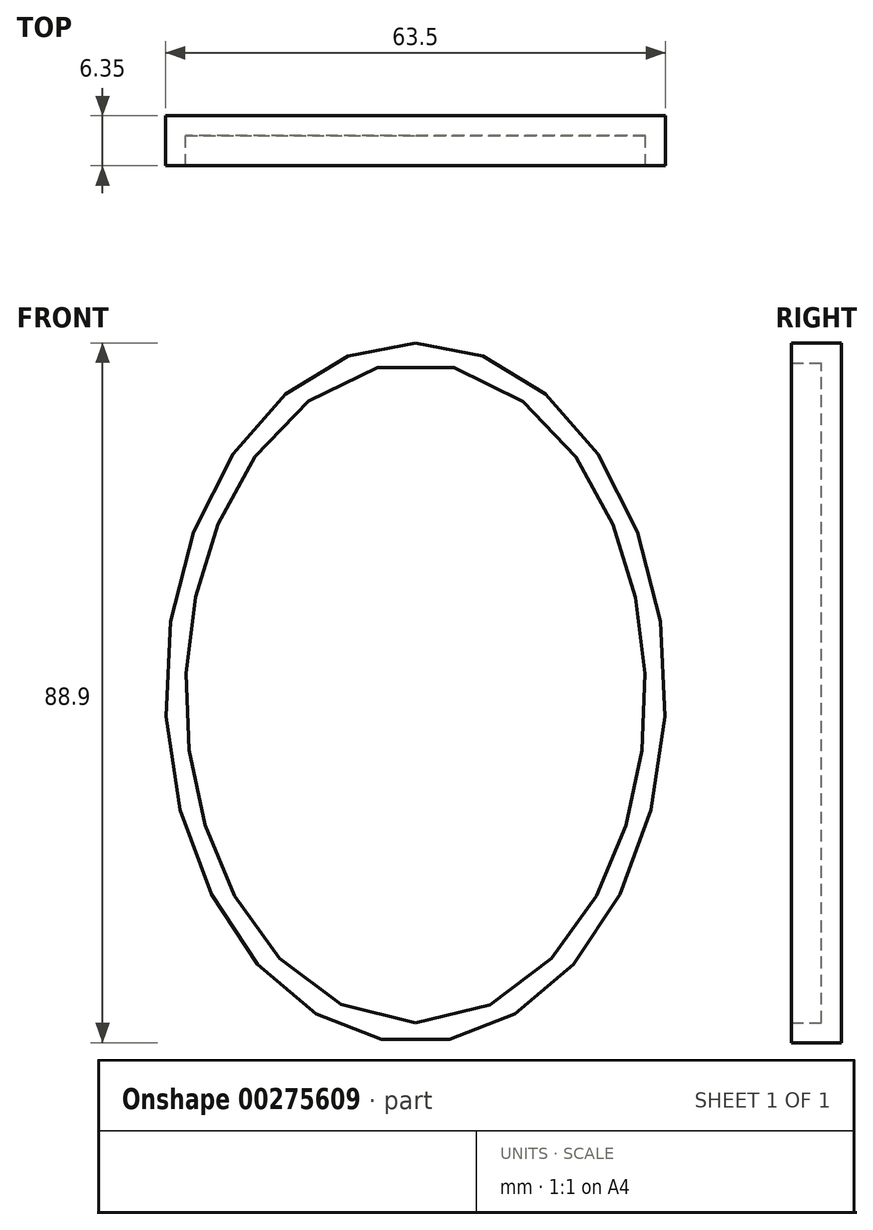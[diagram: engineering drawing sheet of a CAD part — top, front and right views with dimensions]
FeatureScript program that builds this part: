
annotation { "Feature Type Name" : "Feature", "Feature Type Description" : "" }
export const myFeature = defineFeature(function(context is Context, id is Id, definition is map)
    precondition{}
    {
        {
            var Q0;
            Q0=qCreatedBy(makeId("Front.planeOp"),FACE);
            var sketch = newSketch(context, id + "F0", { "sketchPlane" : qUnion([Q0])});
            skEllipse(sketch, "E0", {"center": v(0, 0) * mm, "majorRadius": 44.45 * mm, "minorRadius": 31.75 * mm, "majorAxis": v(0, 1)});
            skSolve(sketch);
        }
        {
            var Q0;
            Q0=makeQuery(id+"F0.imprint","IMPRINT",FACE,{"disambiguationData":[TD([[makeQuery(id+"F0.imprint","IMPRINT",EDGE,{"derivedFrom":sQuery(id+"F0.wireOp",EDGE,"E0")}),1.0]])]});
            extrude(context, id + "F1", {"entities" : qUnion([Q0]), "depth" : 6.35 * mm});
        }
        {
            var Q0;
            Q0=makeQuery(id+"F1.opExtrude","CAP_FACE",FACE,{"disambiguationData":[OSD([sQuery(id+"F0.wireOp",EDGE,"E0")])],"isStart":false});
            shell(context, id + "F2", {"entities" : qUnion([Q0]), "thickness" : 2.54 * mm});
        }
    });
